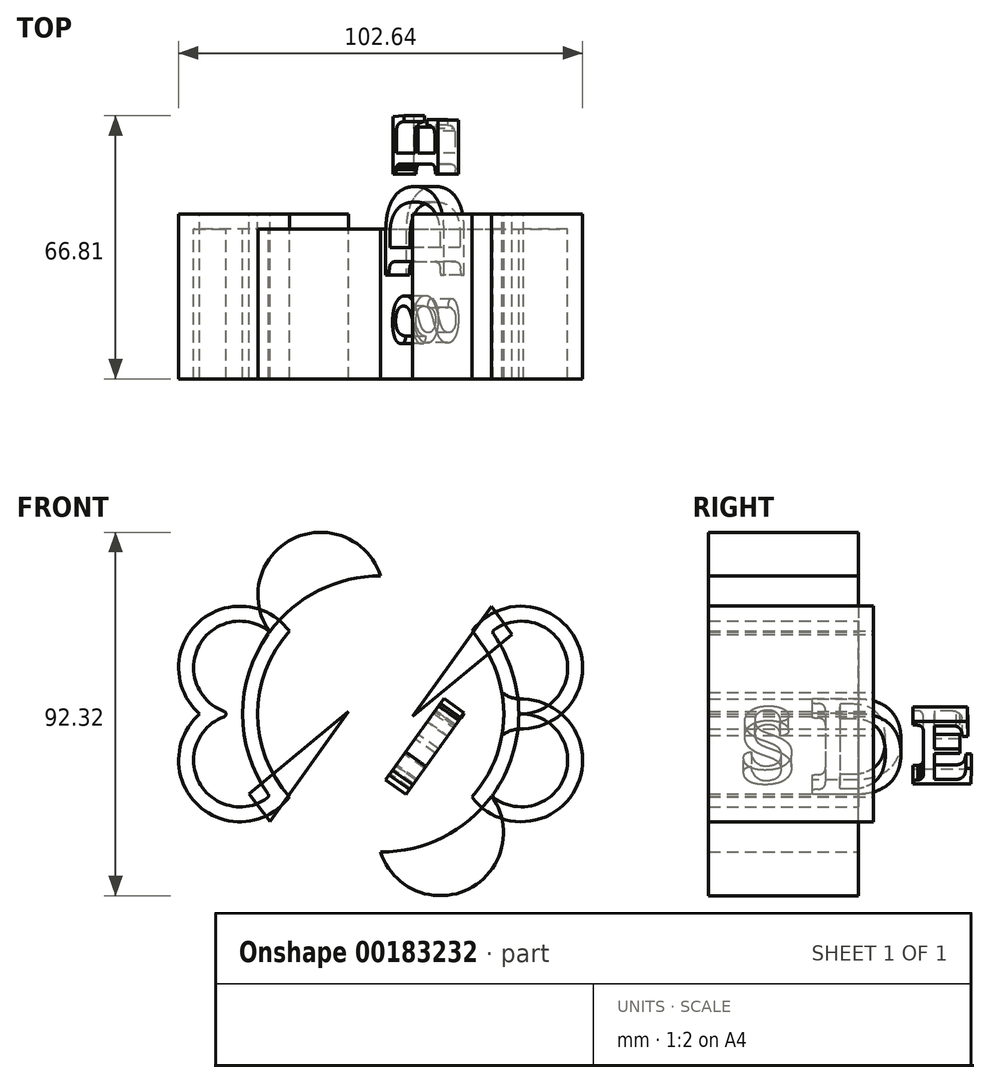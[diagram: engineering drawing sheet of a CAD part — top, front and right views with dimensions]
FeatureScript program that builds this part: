
annotation { "Feature Type Name" : "Feature", "Feature Type Description" : "" }
export const myFeature = defineFeature(function(context is Context, id is Id, definition is map)
    precondition{}
    {
        {
            var Q0;
            Q0=qCreatedBy(makeId("Front.planeOp"),FACE);
            var sketch = newSketch(context, id + "F0", { "sketchPlane" : qUnion([Q0])});
            skCircle(sketch, "E0", {"center": v(0, 0) * mm, "radius": 35.09 * mm});
            skArc(sketch, "E1", {"start": v(0, 35.09) * mm, "mid": v(-22.4, 44.45) * mm, "end": v(-28.2, 20.88) * mm});
            skArc(sketch, "E2.MirrorCS", {"start": v(0, 35.09) * mm, "mid": v(22.4, 44.45) * mm, "end": v(28.2, 20.88) * mm});
            skArc(sketch, "E3.MirrorCS", {"start": v(0, -35.09) * mm, "mid": v(-22.4, -44.45) * mm, "end": v(-28.2, -20.88) * mm});
            skArc(sketch, "E4.MirrorCS", {"start": v(0, -35.09) * mm, "mid": v(22.4, -44.45) * mm, "end": v(28.2, -20.88) * mm});
            skArc(sketch, "E5", {"start": v(-28.2, 20.88) * mm, "mid": v(-46.93, 15.48) * mm, "end": v(-35.09, 0) * mm});
            skArc(sketch, "E6.MirrorCS", {"start": v(28.2, 20.88) * mm, "mid": v(46.93, 15.48) * mm, "end": v(35.09, 0) * mm});
            skArc(sketch, "E7.MirrorCS", {"start": v(-28.2, -20.88) * mm, "mid": v(-46.93, -15.48) * mm, "end": v(-35.09, 0) * mm});
            skArc(sketch, "E8.MirrorCS", {"start": v(28.2, -20.88) * mm, "mid": v(46.93, -15.48) * mm, "end": v(35.09, 0) * mm});
            skSolve(sketch);
        }
        {
            var Q0;
            {var subQ2=sQuery(id+"F0.wireOp",EDGE,"E0");var subQ6=sQuery(id+"F0.wireOp",EDGE,"E2.MirrorCS");var subQ8=sQuery(id+"F0.wireOp",EDGE,"E6.MirrorCS");var subQ9=makeQuery(id+"F0.imprint","INTERSECT",VERTEX,{"derivedFrom":[subQ2,subQ6,subQ8]});Q0=makeQuery(id+"F0.imprint","IMPRINT",FACE,{"disambiguationData":[TD([[makeQuery(id+"F0.imprint","IMPRINT",EDGE,{"disambiguationData":[TD([[subQ9,1.0]])],"derivedFrom":subQ2}),1.0]])]});}
            var Q1;
            {var subQ0=sQuery(id+"F0.wireOp",EDGE,"E5");var subQ3=sQuery(id+"F0.wireOp",EDGE,"E7.MirrorCS");var subQ5=makeQuery(id+"F0.imprint","INTERSECT",VERTEX,{"derivedFrom":[subQ0,subQ3]});Q1=makeQuery(id+"F0.imprint","IMPRINT",FACE,{"disambiguationData":[TD([[makeQuery(id+"F0.imprint","IMPRINT",EDGE,{"disambiguationData":[TD([[subQ5,1.0]])],"derivedFrom":subQ0}),1.0]])]});}
            var Q2;
            {var subQ0=sQuery(id+"F0.wireOp",EDGE,"E6.MirrorCS");var subQ3=sQuery(id+"F0.wireOp",EDGE,"E8.MirrorCS");var subQ5=makeQuery(id+"F0.imprint","INTERSECT",VERTEX,{"derivedFrom":[subQ0,subQ3]});Q2=makeQuery(id+"F0.imprint","IMPRINT",FACE,{"disambiguationData":[TD([[makeQuery(id+"F0.imprint","IMPRINT",EDGE,{"disambiguationData":[TD([[subQ5,1.0]])],"derivedFrom":subQ0}),-1.0]])]});}
            var Q3;
            {var subQ0=sQuery(id+"F0.wireOp",EDGE,"E3.MirrorCS");Q3=makeQuery(id+"F0.imprint","IMPRINT",FACE,{"disambiguationData":[TD([[makeQuery(id+"F0.imprint","IMPRINT",EDGE,{"derivedFrom":subQ0}),-1.0]])]});}
            var Q4;
            {var subQ0=sQuery(id+"F0.wireOp",EDGE,"E7.MirrorCS");var subQ3=sQuery(id+"F0.wireOp",EDGE,"E5");var subQ5=makeQuery(id+"F0.imprint","INTERSECT",VERTEX,{"derivedFrom":[subQ3,subQ0]});Q4=makeQuery(id+"F0.imprint","IMPRINT",FACE,{"disambiguationData":[TD([[makeQuery(id+"F0.imprint","IMPRINT",EDGE,{"disambiguationData":[TD([[subQ5,-1.0]])],"derivedFrom":subQ3}),-1.0]])]});}
            var Q5;
            {var subQ0=sQuery(id+"F0.wireOp",EDGE,"E8.MirrorCS");var subQ3=sQuery(id+"F0.wireOp",EDGE,"E6.MirrorCS");var subQ5=makeQuery(id+"F0.imprint","INTERSECT",VERTEX,{"derivedFrom":[subQ3,subQ0]});Q5=makeQuery(id+"F0.imprint","IMPRINT",FACE,{"disambiguationData":[TD([[makeQuery(id+"F0.imprint","IMPRINT",EDGE,{"disambiguationData":[TD([[subQ5,-1.0]])],"derivedFrom":subQ3}),1.0]])]});}
            var Q6;
            {var subQ0=sQuery(id+"F0.wireOp",EDGE,"E4.MirrorCS");Q6=makeQuery(id+"F0.imprint","IMPRINT",FACE,{"disambiguationData":[TD([[makeQuery(id+"F0.imprint","IMPRINT",EDGE,{"derivedFrom":subQ0}),1.0]])]});}
            var Q7;
            {var subQ0=sQuery(id+"F0.wireOp",EDGE,"E1");Q7=makeQuery(id+"F0.imprint","IMPRINT",FACE,{"disambiguationData":[TD([[makeQuery(id+"F0.imprint","IMPRINT",EDGE,{"derivedFrom":subQ0}),1.0]])]});}
            var Q8;
            {var subQ0=sQuery(id+"F0.wireOp",EDGE,"E2.MirrorCS");Q8=makeQuery(id+"F0.imprint","IMPRINT",FACE,{"disambiguationData":[TD([[makeQuery(id+"F0.imprint","IMPRINT",EDGE,{"derivedFrom":subQ0}),-1.0]])]});}
            var Q9;
            {var subQ0=sQuery(id+"F0.wireOp",EDGE,"E8.MirrorCS");var subQ1=sQuery(id+"F0.wireOp",EDGE,"E6.MirrorCS");var subQ3=makeQuery(id+"F0.imprint","INTERSECT",VERTEX,{"derivedFrom":[subQ1,subQ0]});Q9=makeQuery(id+"F0.imprint","IMPRINT",FACE,{"disambiguationData":[TD([[makeQuery(id+"F0.imprint","IMPRINT",EDGE,{"disambiguationData":[TD([[subQ3,-1.0]])],"derivedFrom":subQ1}),-1.0]])]});}
            var Q10;
            {var subQ0=sQuery(id+"F0.wireOp",EDGE,"E7.MirrorCS");var subQ1=sQuery(id+"F0.wireOp",EDGE,"E5");var subQ3=makeQuery(id+"F0.imprint","INTERSECT",VERTEX,{"derivedFrom":[subQ1,subQ0]});Q10=makeQuery(id+"F0.imprint","IMPRINT",FACE,{"disambiguationData":[TD([[makeQuery(id+"F0.imprint","IMPRINT",EDGE,{"disambiguationData":[TD([[subQ3,-1.0]])],"derivedFrom":subQ1}),1.0]])]});}
            extrude(context, id + "F1", {"entities" : qUnion([Q0, Q1, Q2, Q3, Q4, Q5, Q6, Q7, Q8, Q9, Q10]), "depth" : 38.1 * mm});
        }
        {
            var Q0;
            Q0=makeQuery(id+"F1.opExtrude","CAP_FACE",FACE,{"disambiguationData":[OSD([sQuery(id+"F0.wireOp",EDGE,"E1"),sQuery(id+"F0.wireOp",EDGE,"E2.MirrorCS"),sQuery(id+"F0.wireOp",EDGE,"E3.MirrorCS"),sQuery(id+"F0.wireOp",EDGE,"E4.MirrorCS"),sQuery(id+"F0.wireOp",EDGE,"E5"),sQuery(id+"F0.wireOp",EDGE,"E6.MirrorCS"),sQuery(id+"F0.wireOp",EDGE,"E7.MirrorCS"),sQuery(id+"F0.wireOp",EDGE,"E8.MirrorCS")])],"isStart":false});
            shell(context, id + "F2", {"entities" : qUnion([Q0]), "thickness" : 3.8 * mm, "oppositeDirection" : true});
        }
        {
            var Q0;
            Q0=makeQuery(id+"F2.opShell","OFFSET_EDGE",EDGE,{"disambiguationData":[OSD([sQuery(id+"F0.wireOp",EDGE,"E0"),sQuery(id+"F0.wireOp",EDGE,"E1"),sQuery(id+"F0.wireOp",EDGE,"E5")])]});
            var Q1;
            Q1=makeQuery(id+"F2.opShell","OFFSET_EDGE",EDGE,{"disambiguationData":[OSD([sQuery(id+"F0.wireOp",EDGE,"E5"),sQuery(id+"F0.wireOp",EDGE,"E7.MirrorCS")])]});
            var Q2;
            Q2=makeQuery(id+"F2.opShell","OFFSET_EDGE",EDGE,{"disambiguationData":[OSD([sQuery(id+"F0.wireOp",EDGE,"E0"),sQuery(id+"F0.wireOp",EDGE,"E3.MirrorCS"),sQuery(id+"F0.wireOp",EDGE,"E7.MirrorCS")])]});
            var Q3;
            Q3=makeQuery(id+"F2.opShell","OFFSET_EDGE",EDGE,{"disambiguationData":[OSD([sQuery(id+"F0.wireOp",EDGE,"E0"),sQuery(id+"F0.wireOp",EDGE,"E1"),sQuery(id+"F0.wireOp",EDGE,"E2.MirrorCS")])]});
            var Q4;
            Q4=makeQuery(id+"F2.opShell","OFFSET_EDGE",EDGE,{"disambiguationData":[OSD([sQuery(id+"F0.wireOp",EDGE,"E0"),sQuery(id+"F0.wireOp",EDGE,"E2.MirrorCS"),sQuery(id+"F0.wireOp",EDGE,"E6.MirrorCS")])]});
            var Q5;
            Q5=makeQuery(id+"F2.opShell","OFFSET_EDGE",EDGE,{"disambiguationData":[OSD([sQuery(id+"F0.wireOp",EDGE,"E6.MirrorCS"),sQuery(id+"F0.wireOp",EDGE,"E8.MirrorCS")])]});
            var Q6;
            Q6=makeQuery(id+"F2.opShell","OFFSET_EDGE",EDGE,{"disambiguationData":[OSD([sQuery(id+"F0.wireOp",EDGE,"E0"),sQuery(id+"F0.wireOp",EDGE,"E4.MirrorCS"),sQuery(id+"F0.wireOp",EDGE,"E8.MirrorCS")])]});
            var Q7;
            Q7=makeQuery(id+"F2.opShell","OFFSET_EDGE",EDGE,{"disambiguationData":[OSD([sQuery(id+"F0.wireOp",EDGE,"E0"),sQuery(id+"F0.wireOp",EDGE,"E3.MirrorCS"),sQuery(id+"F0.wireOp",EDGE,"E4.MirrorCS")])]});
            fillet(context, id + "F3", {"entities" : qUnion([Q0, Q1, Q2, Q3, Q4, Q5, Q6, Q7]), "radius" : 0.76 * mm, "tangentPropagation" : true, "allowEdgeOverflow" : false});
        }
        {
            var Q0;
            Q0=makeQuery(id+"F2.opShell","OFFSET_FACE",FACE,{"disambiguationData":[OSD([sQuery(id+"F0.wireOp",EDGE,"E1"),sQuery(id+"F0.wireOp",EDGE,"E2.MirrorCS"),sQuery(id+"F0.wireOp",EDGE,"E3.MirrorCS"),sQuery(id+"F0.wireOp",EDGE,"E4.MirrorCS"),sQuery(id+"F0.wireOp",EDGE,"E5"),sQuery(id+"F0.wireOp",EDGE,"E6.MirrorCS"),sQuery(id+"F0.wireOp",EDGE,"E7.MirrorCS"),sQuery(id+"F0.wireOp",EDGE,"E8.MirrorCS")])]});
            var sketch = newSketch(context, id + "F4", { "sketchPlane" : qUnion([Q0])});
            skText(sketch, "E9", { "text": "S    E", "fontName": "NotoSerif-Regular.ttf"});
            const initialGuessF4  = {"E9": [-0.03051, -0.00957, 1, 0, 0.0197]};
            skSetInitialGuess(sketch, initialGuessF4);
            skSolve(sketch);
        }
        {
            var Q0;
            Q0=makeQuery(id+"F2.opShell","OFFSET_FACE",FACE,{"disambiguationData":[OSD([sQuery(id+"F0.wireOp",EDGE,"E1"),sQuery(id+"F0.wireOp",EDGE,"E2.MirrorCS"),sQuery(id+"F0.wireOp",EDGE,"E3.MirrorCS"),sQuery(id+"F0.wireOp",EDGE,"E4.MirrorCS"),sQuery(id+"F0.wireOp",EDGE,"E5"),sQuery(id+"F0.wireOp",EDGE,"E6.MirrorCS"),sQuery(id+"F0.wireOp",EDGE,"E7.MirrorCS"),sQuery(id+"F0.wireOp",EDGE,"E8.MirrorCS")])]});
            var sketch = newSketch(context, id + "F5", { "sketchPlane" : qUnion([Q0])});
            skText(sketch, "E10", { "text": "D", "fontName": "NotoSerif-Regular.ttf"});
            const initialGuessF5  = {"E10": [-0.01308, -0.01284, 1, 0, 0.02562]};
            skSetInitialGuess(sketch, initialGuessF5);
            skSolve(sketch);
        }
        {
            var Q0;
            Q0 = qSketchRegion(id + "F4", true);
            var Q1;
            Q1 = qSketchRegion(id + "F5", true);
            extrude(context, id + "F6", {"entities" : qUnion([Q0, Q1]), "operationType" : NewBodyOperationType.ADD, "depth" : 6.35 * mm});
        }
    });
